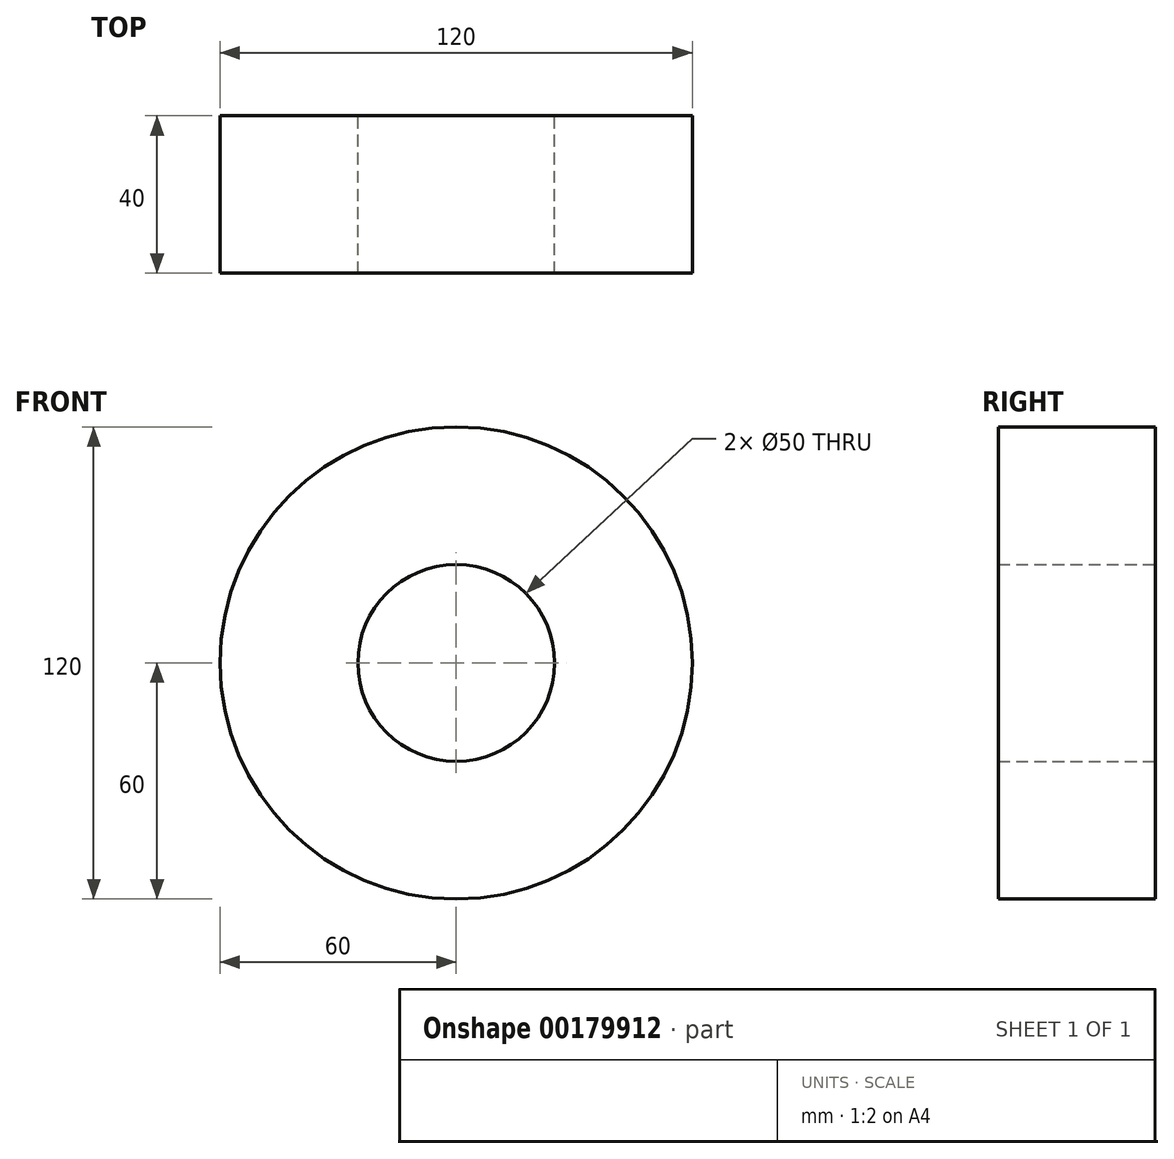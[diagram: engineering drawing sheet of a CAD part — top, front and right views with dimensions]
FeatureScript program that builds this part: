
annotation { "Feature Type Name" : "Feature", "Feature Type Description" : "" }
export const myFeature = defineFeature(function(context is Context, id is Id, definition is map)
    precondition{}
    {
        {
            var Q0;
            Q0=qCreatedBy(makeId("Front.planeOp"),FACE);
            var sketch = newSketch(context, id + "F0", { "sketchPlane" : qUnion([Q0])});
            skCircle(sketch, "E0", {"center": v(0, 0) * mm, "radius": 60 * mm});
            skCircle(sketch, "E1", {"center": v(0, 0) * mm, "radius": 25 * mm});
            skSolve(sketch);
        }
        {
            var Q0;
            Q0=makeQuery(id+"F0.imprint","IMPRINT",FACE,{"disambiguationData":[TD([[makeQuery(id+"F0.imprint","IMPRINT",EDGE,{"derivedFrom":sQuery(id+"F0.wireOp",EDGE,"E0")}),1.0]])]});
            extrude(context, id + "F1", {"entities" : qUnion([Q0]), "depth" : 40 * mm});
        }
        {
            var Q0;
            Q0=makeQuery(id+"F1.opExtrude","SWEPT_BODY",BODY,{"disambiguationData":[OSD([sQuery(id+"F0.wireOp",EDGE,"E0"),sQuery(id+"F0.wireOp",EDGE,"E1")])]});
            transform(context, id + "F2", {"entities" : qUnion([Q0]), "transformType" : TransformType.TRANSLATION_3D, "dx" : 0 * mm, "dy" : 0 * mm, "dz" : 0 * mm, "makeCopy" : true});
        }
    });
